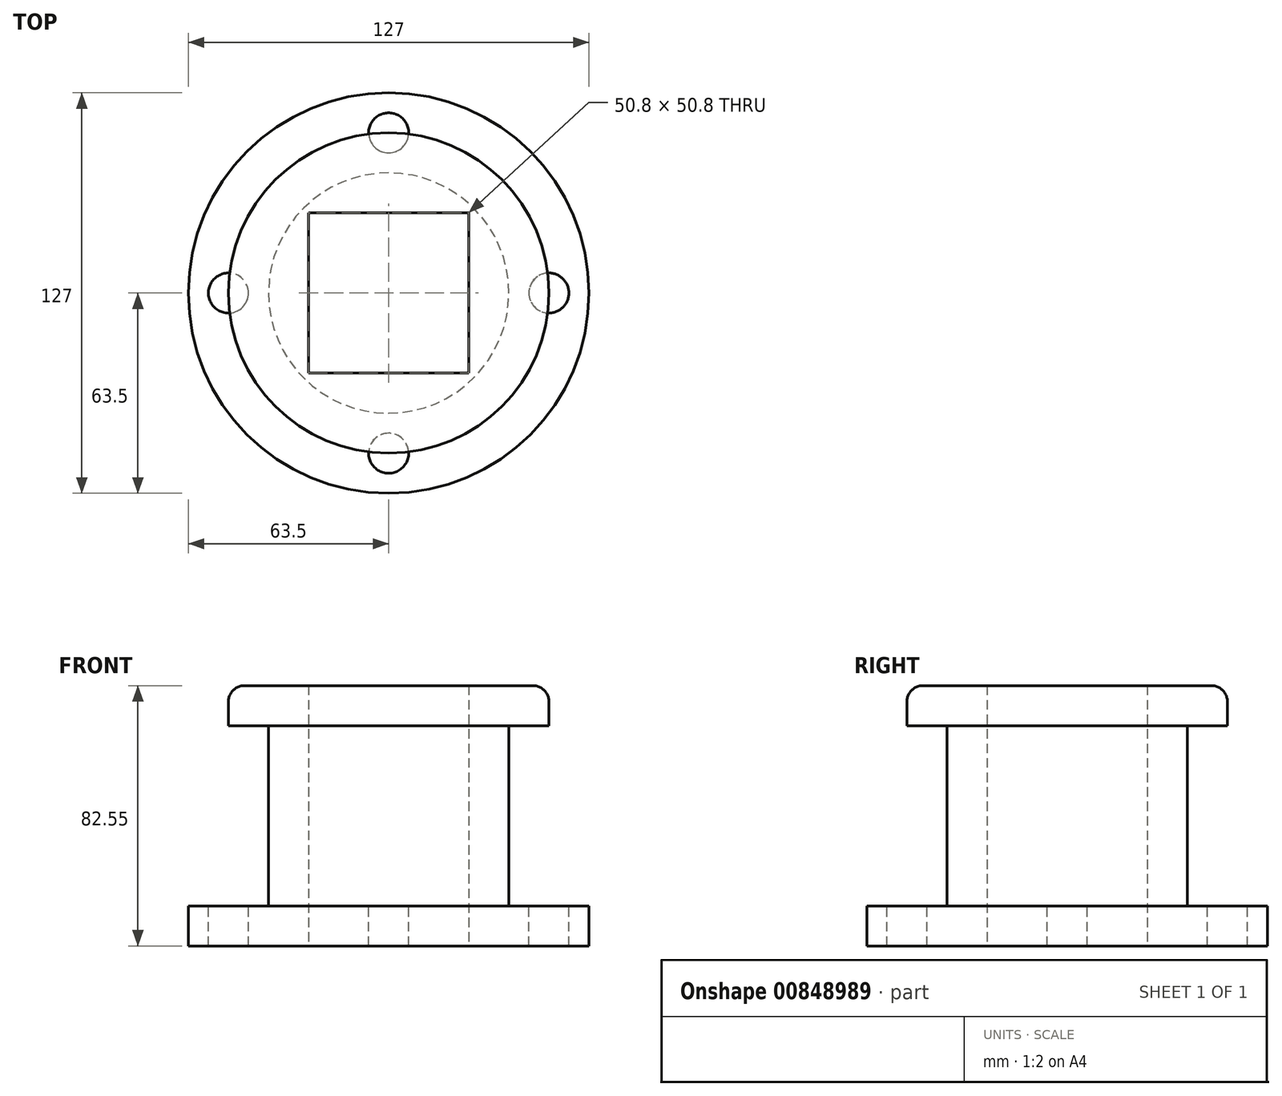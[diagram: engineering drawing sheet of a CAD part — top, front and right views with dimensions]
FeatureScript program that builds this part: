
annotation { "Feature Type Name" : "Feature", "Feature Type Description" : "" }
export const myFeature = defineFeature(function(context is Context, id is Id, definition is map)
    precondition{}
    {
        {
            var Q0;
            Q0=qCreatedBy(makeId("Top.planeOp"),FACE);
            var sketch = newSketch(context, id + "F0", { "sketchPlane" : qUnion([Q0])});
            skCircle(sketch, "E0", {"center": v(0, 0) * mm, "radius": 38.1 * mm});
            skSolve(sketch);
        }
        {
            var Q0;
            Q0=qSketchRegion(id+"F0",true);
            extrude(context, id + "F1", {"entities" : qUnion([Q0]), "oppositeDirection" : true, "depth" : 57.15 * mm, "offsetDistance" : 25.4 * mm});
        }
        {
            var Q0;
            Q0=qCreatedBy(makeId("Top.planeOp"),FACE);
            var sketch = newSketch(context, id + "F2", { "sketchPlane" : qUnion([Q0])});
            skCircle(sketch, "E1", {"center": v(0, 0) * mm, "radius": 50.8 * mm});
            skSolve(sketch);
        }
        {
            var Q0;
            Q0=qSketchRegion(id+"F2",true);
            extrude(context, id + "F3", {"entities" : qUnion([Q0]), "operationType" : NewBodyOperationType.ADD, "depth" : 12.7 * mm, "offsetDistance" : 25.4 * mm});
        }
        {
            var Q0;
            Q0=makeQuery(id+"F3.opExtrude","CAP_EDGE",EDGE,{"disambiguationData":[OSD([sQuery(id+"F2.wireOp",EDGE,"E1")])],"isStart":false});
            fillet(context, id + "F4", {"entities" : qUnion([Q0]), "radius" : 5.08 * mm, "tangentPropagation" : true, "allowEdgeOverflow" : false});
        }
        {
            var Q0;
            Q0=qCreatedBy(makeId("Top.planeOp"),FACE);
            var sketch = newSketch(context, id + "F5", { "sketchPlane" : qUnion([Q0])});
            skCircle(sketch, "E2", {"center": v(0, 0) * mm, "radius": 63.5 * mm});
            skSolve(sketch);
        }
        {
            var Q0;
            Q0=qSketchRegion(id+"F5",true);
            extrude(context, id + "F6", {"entities" : qUnion([Q0]), "operationType" : NewBodyOperationType.ADD, "oppositeDirection" : true, "depth" : 69.85 * mm, "offsetDistance" : 25.4 * mm, "hasSecondDirection" : true, "secondDirectionOppositeDirection" : true, "secondDirectionDepth" : 57.15 * mm});
        }
        {
            var Q0;
            Q0=qCreatedBy(makeId("Top.planeOp"),FACE);
            var sketch = newSketch(context, id + "F7", { "sketchPlane" : qUnion([Q0])});
            skLineSegment(sketch, "E3.bottom", {"start": v(25.4, -25.4) * mm, "end": v(-25.4, -25.4) * mm});
            skLineSegment(sketch, "E3.top", {"start": v(25.4, 25.4) * mm, "end": v(-25.4, 25.4) * mm});
            skLineSegment(sketch, "E3.left", {"start": v(25.4, -25.4) * mm, "end": v(25.4, 25.4) * mm});
            skLineSegment(sketch, "E3.right", {"start": v(-25.4, -25.4) * mm, "end": v(-25.4, 25.4) * mm});
            skPoint(sketch, "E3.middle", {"position": v(0, 0) * mm});
            skSolve(sketch);
        }
        {
            var Q0;
            Q0=qSketchRegion(id+"F7",true);
            extrude(context, id + "F8", {"entities" : qUnion([Q0]), "operationType" : NewBodyOperationType.REMOVE, "depth" : 25.4 * mm, "offsetDistance" : 25.4 * mm, "hasSecondDirection" : true, "secondDirectionOppositeDirection" : true, "secondDirectionDepth" : 109.73 * mm});
        }
        {
            var Q0;
            Q0=qCreatedBy(makeId("Top.planeOp"),FACE);
            var sketch = newSketch(context, id + "F9", { "sketchPlane" : qUnion([Q0])});
            skCircle(sketch, "E4", {"center": v(0, -50.8) * mm, "radius": 6.35 * mm});
            skCircle(sketch, "E5", {"center": v(-50.8, 0) * mm, "radius": 6.35 * mm});
            skCircle(sketch, "E6", {"center": v(50.8, 0) * mm, "radius": 6.35 * mm});
            skCircle(sketch, "E7", {"center": v(0, 50.8) * mm, "radius": 6.35 * mm});
            skSolve(sketch);
        }
        {
            var Q0;
            Q0=qSketchRegion(id+"F9",true);
            extrude(context, id + "F10", {"entities" : qUnion([Q0]), "operationType" : NewBodyOperationType.REMOVE, "oppositeDirection" : true, "depth" : 103.89 * mm, "offsetDistance" : 25.4 * mm, "hasSecondDirection" : true, "secondDirectionOppositeDirection" : true, "secondDirectionDepth" : 38.35 * mm});
        }
    });
